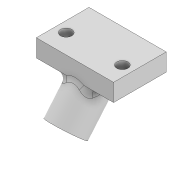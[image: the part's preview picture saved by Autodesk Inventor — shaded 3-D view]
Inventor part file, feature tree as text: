
AUTODESK INVENTOR PART (.ipt)
format: ipt  version: 2022 (Build 260153000, 153)  size: 231,424 bytes
history: native  units: mm
features: extrude x7, sketch x6, projected_geometry x3, plane x2, fillet x1
ambient origin geometry x8: Origin, YZ Plane, XZ Plane, XY Plane, X Axis, Y Axis, Z Axis, Center Point
bodies: Body1 (feature_tree)
feature tree (19):
  sketch  "Sketch6"  dims[d29=22.0mm d30=15.0mm]
  extrude  "Extrusion6"  Depth=15.0mm
  plane  "Work Plane3"
  extrude  "Extrusion7"  [1 undecoded]
  extrude  "Extrusion9"  Depth=5.0mm
  extrude  "Extrusion12"  Depth=10.0mm
  fillet  "Fillet4"  Radius=10.0mm
  plane  "Work Plane4"
  sketch  "Sketch16"  dims[d43=3.2mm d44=3.2mm]
  extrude  "Extrusion14"  Depth=3.2mm
  extrude  "Extrusion15"  Depth=10.0mm
  extrude  "Extrusion16"  Depth=10.0mm
  sketch  "Sketch7"  dims[d31=5.0mm d32=0.0mm d33=-6.981317mm]
  sketch  "Sketch9"  dims[d34=5.5mm d35=5.0mm]
  sketch  "Sketch12"  dims[d36=11.0mm d37=10.0mm d38=10.0mm d39=0.0mm]
  projected_geometry  "Projected Loop4"
  projected_geometry  "Projected Loop5"
  sketch  "Sketch17"  dims[d45=5.5mm d46=5.5mm d47=3.0mm d48=3.0mm d49=10.0mm d50=0.0mm d51=20.0mm d52=0.0mm d59=100.0mm d60=0.0mm d61=2.0mm d66=-15.0mm d67=15.0mm d68=0.0mm d69=6.0mm d70=0.0mm d71=100.0mm d72=0.0mm d12=0.5mm d13=0.872665mm d14=0.5mm d15=0.872665mm]
  projected_geometry  "Projected Loop6"
note: 1 required parameter value undecoded (feature->parameter linkage not recoverable at this tier; creation-order binding heuristic only, values carry confidence <= 0.55)
